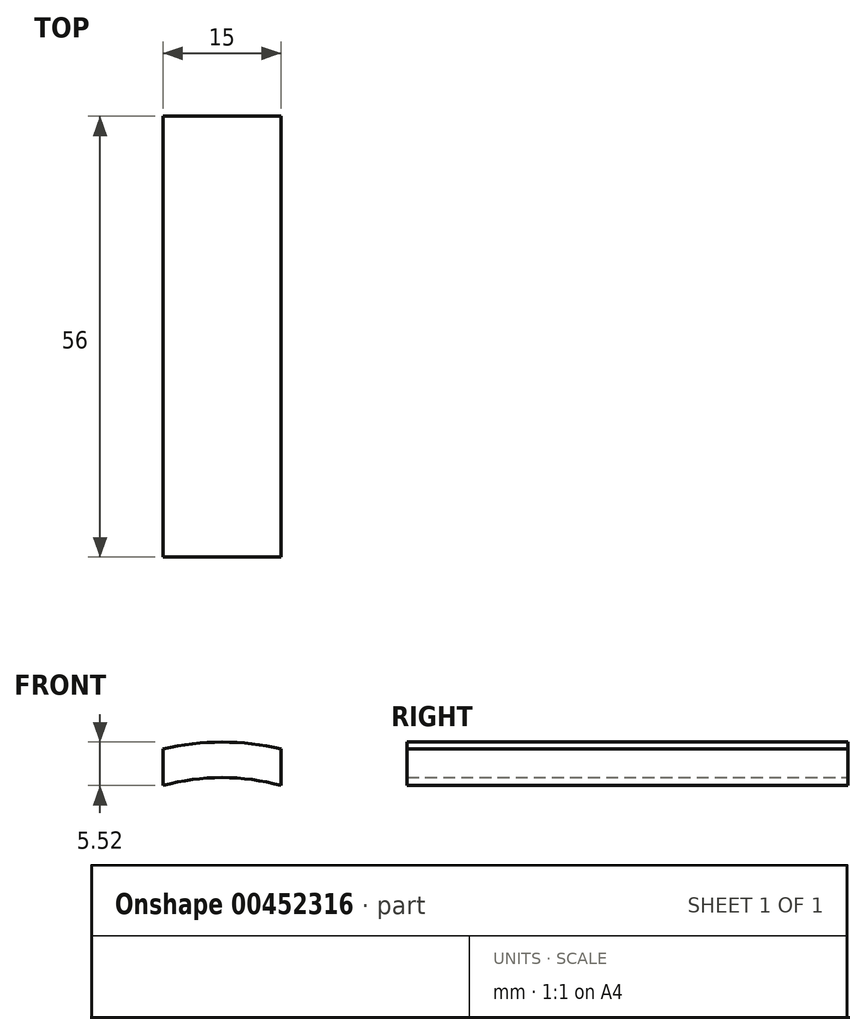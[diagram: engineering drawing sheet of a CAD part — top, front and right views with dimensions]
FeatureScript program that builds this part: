
annotation { "Feature Type Name" : "Feature", "Feature Type Description" : "" }
export const myFeature = defineFeature(function(context is Context, id is Id, definition is map)
    precondition{}
    {
        {
            var Q0;
            Q0=qCreatedBy(makeId("Front.planeOp"),FACE);
            var sketch = newSketch(context, id + "F0", { "sketchPlane" : qUnion([Q0])});
            skArc(sketch, "E0", {"start": v(7.5, 31.62) * mm, "mid": v(0, 32.5) * mm, "end": v(-7.5, 31.62) * mm});
            skArc(sketch, "E1", {"start": v(7.5, 26.98) * mm, "mid": v(0, 28) * mm, "end": v(-7.5, 26.98) * mm});
            skLineSegment(sketch, "E2.left", {"start": v(7.5, 26.98) * mm, "end": v(7.5, 31.62) * mm});
            skPoint(sketch, "E2.middle", {"position": v(0, 32.5) * mm});
            skPoint(sketch, "E3.orphan", {"position": v(7.5, 18.43) * mm});
            skPoint(sketch, "E4.orphan", {"position": v(-7.5, 18.43) * mm});
            skLineSegment(sketch, "E5", {"start": v(-7.5, 31.62) * mm, "end": v(-7.5, 26.98) * mm});
            skPoint(sketch, "E2.top.end.orphan", {"position": v(-7.5, 46.57) * mm});
            skPoint(sketch, "E2.top.start.orphan", {"position": v(7.5, 46.57) * mm});
            skSolve(sketch);
        }
        {
            var Q0;
            Q0 = qSketchRegion(id + "F0", true);
            extrude(context, id + "F1", {"entities" : qUnion([Q0]), "depth" : 56 * mm});
        }
    });
